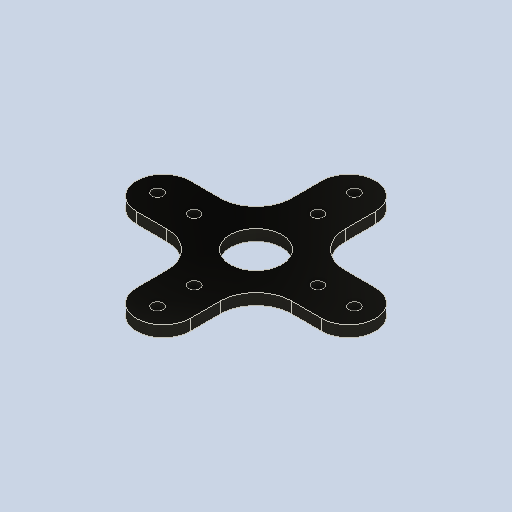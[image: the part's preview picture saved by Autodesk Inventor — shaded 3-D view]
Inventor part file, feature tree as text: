
AUTODESK INVENTOR PART (.ipt)
format: ipt  version: 2025.1 (Build 291241020, 241B)  size: 171,008 bytes
history: native  units: in
note: dims shown in document units (in); Inventor stores cm internally (conversion verified against a paired STEP export)
features: sketch x2, extrude x1, other x1
ambient origin geometry x8: Origin, YZ Plane, XZ Plane, XY Plane, X Axis, Y Axis, Z Axis, Center Point
bodies: Solid1 (feature_tree)
feature tree (4):
  extrude  "Extrusion1"  Depth=0.1575in
  sketch  "Sketch1"  dims[d0=1.5748in d2=360.0deg d4=0.1575in]
  sketch  "Sketch Circular Pattern1"  dims[d5=0.8661in d6=1.378in d7=0.7232in d39=0.375in d41=0.375in d46=0.5in d50=0.1575in d51=0.0in]
  other  "Image1"
